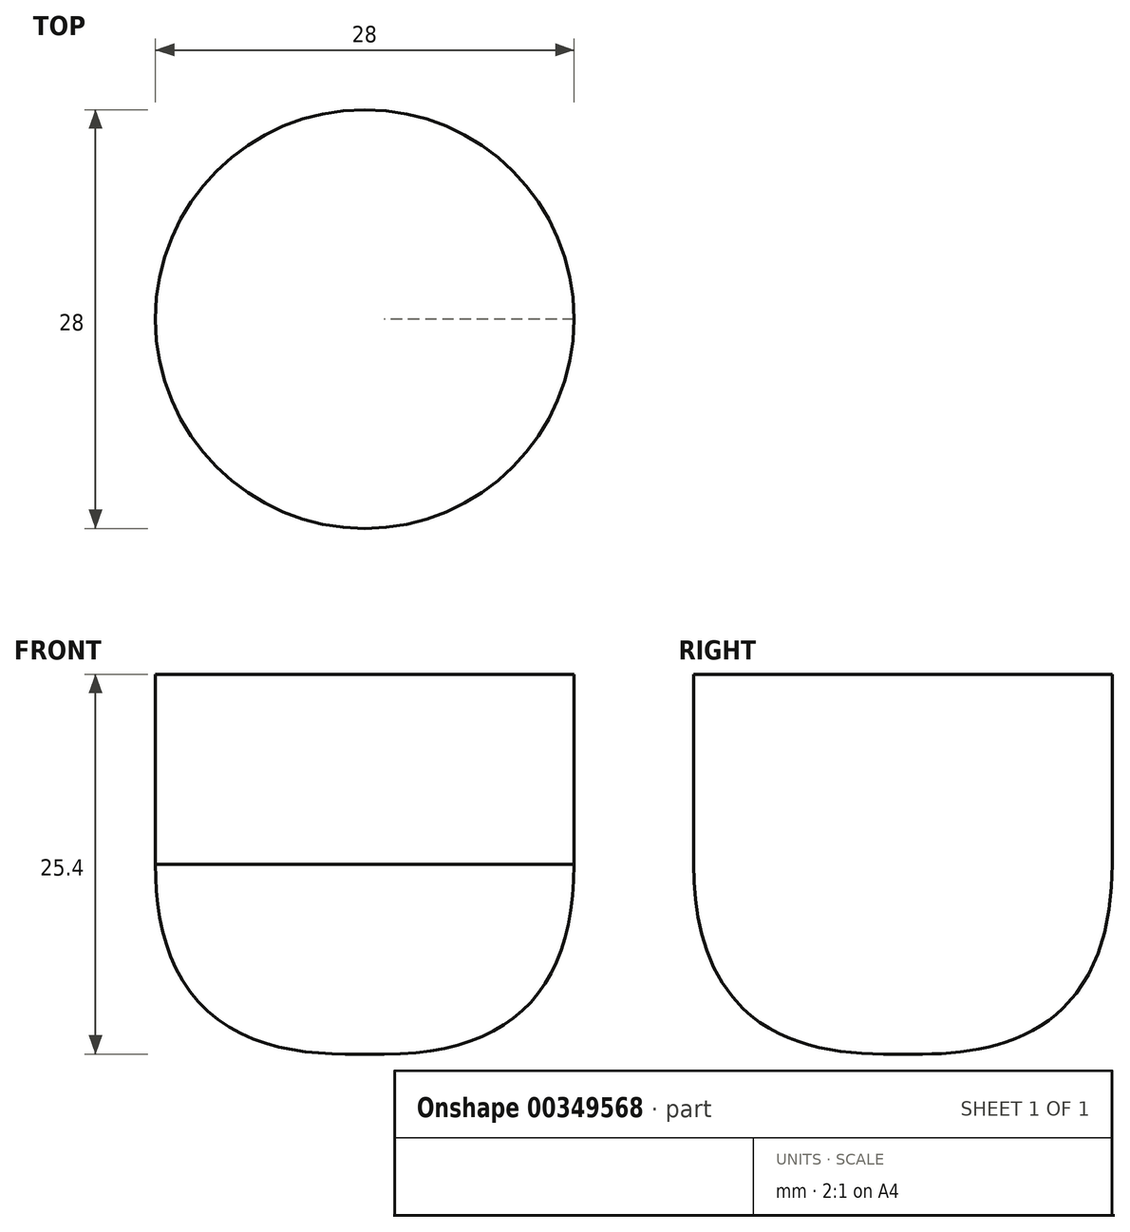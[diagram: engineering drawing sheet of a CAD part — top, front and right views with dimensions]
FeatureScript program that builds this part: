
annotation { "Feature Type Name" : "Feature", "Feature Type Description" : "" }
export const myFeature = defineFeature(function(context is Context, id is Id, definition is map)
    precondition{}
    {
        {
            var Q0;
            Q0=qCreatedBy(makeId("Top.planeOp"),FACE);
            var sketch = newSketch(context, id + "F0", { "sketchPlane" : qUnion([Q0])});
            skCircle(sketch, "E0", {"center": v(0, 0) * mm, "radius": 14 * mm});
            skSolve(sketch);
        }
        {
            var Q0;
            Q0 = qSketchRegion(id + "F0", true);
            extrude(context, id + "F1", {"entities" : qUnion([Q0]), "depth" : 25.4 * mm});
        }
        {
            var Q0;
            Q0=makeQuery(id+"F1.opExtrude","CAP_FACE",FACE,{"disambiguationData":[OSD([sQuery(id+"F0.wireOp",EDGE,"E0")])],"isStart":true});
            fillet(context, id + "F2", {"entities" : qUnion([Q0]), "radius" : 12.7 * mm, "tangentPropagation" : true, "rho" : .5, "crossSection" : FilletCrossSection.CONIC, "allowEdgeOverflow" : false});
        }
    });
